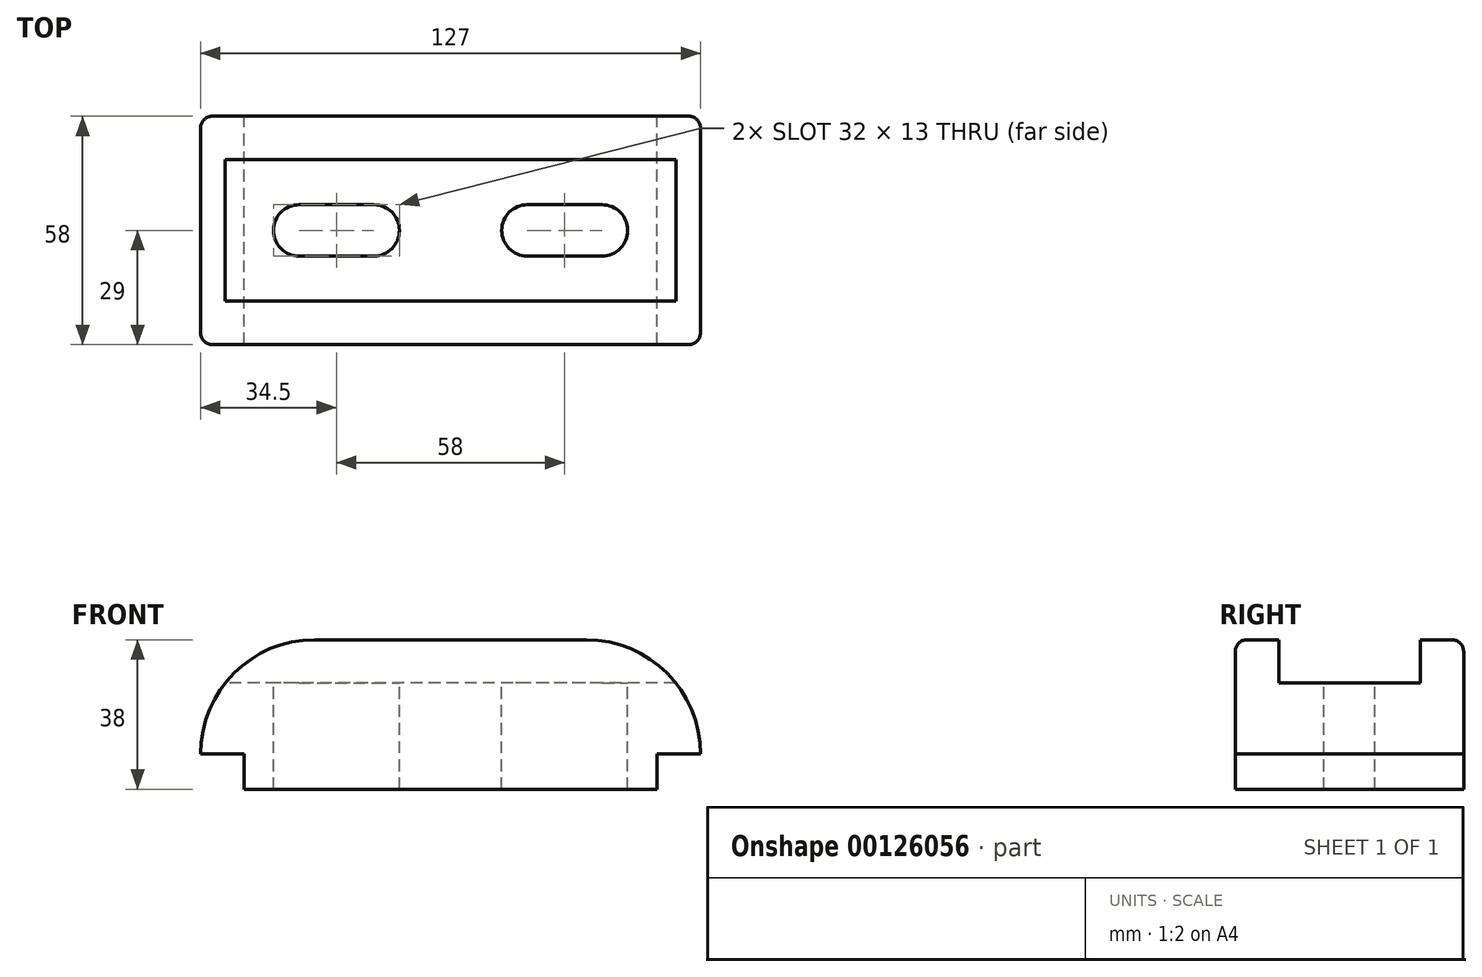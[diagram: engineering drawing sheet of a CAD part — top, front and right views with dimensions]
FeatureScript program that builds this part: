
annotation { "Feature Type Name" : "Feature", "Feature Type Description" : "" }
export const myFeature = defineFeature(function(context is Context, id is Id, definition is map)
    precondition{}
    {
        {
            var Q0;
            Q0=qCreatedBy(makeId("Front.planeOp"),FACE);
            var sketch = newSketch(context, id + "F0", { "sketchPlane" : qUnion([Q0])});
            skLineSegment(sketch, "E0", {"start": v(0, 0) * mm, "end": v(0, 9) * mm});
            skLineSegment(sketch, "E1", {"start": v(0, 9) * mm, "end": v(11, 9) * mm});
            skLineSegment(sketch, "E2", {"start": v(11, 9) * mm, "end": v(11, 9) * mm});
            skLineSegment(sketch, "E3", {"start": v(-18, 38) * mm, "end": v(-87, 38) * mm});
            skLineSegment(sketch, "E4", {"start": v(-116, 9) * mm, "end": v(-116, 9) * mm});
            skLineSegment(sketch, "E5", {"start": v(-116, 9) * mm, "end": v(-105, 9) * mm});
            skLineSegment(sketch, "E6", {"start": v(-105, 9) * mm, "end": v(-105, 0) * mm});
            skLineSegment(sketch, "E7", {"start": v(-105, 0) * mm, "end": v(0, 0) * mm});
            skPoint(sketch, "E8.visualSharp", {"position": v(-116, 38) * mm});
            skArc(sketch, "E8.filletArc", {"start": v(-87, 38) * mm, "mid": v(-107.5, 29.5) * mm, "end": v(-116, 9) * mm});
            skPoint(sketch, "E9.visualSharp", {"position": v(11, 38) * mm});
            skArc(sketch, "E9.filletArc", {"start": v(11, 9) * mm, "mid": v(2.5, 29.5) * mm, "end": v(-18, 38) * mm});
            skSolve(sketch);
        }
        {
            var Q0;
            Q0 = qSketchRegion(id + "F0", true);
            extrude(context, id + "F1", {"entities" : qUnion([Q0]), "endBound" : BoundingType.SYMMETRIC, "depth" : 58 * mm});
        }
        {
            var Q0;
            Q0=makeQuery(id+"F1.opExtrude","SWEPT_FACE",FACE,{"disambiguationData":[OSD([sQuery(id+"F0.wireOp",EDGE,"E3")])]});
            var sketch = newSketch(context, id + "F2", { "sketchPlane" : qUnion([Q0])});
            skLineSegment(sketch, "E10", {"start": v(-128, 18) * mm, "end": v(22, 18) * mm});
            skLineSegment(sketch, "E11", {"start": v(22, 18) * mm, "end": v(22, -18) * mm});
            skLineSegment(sketch, "E12", {"start": v(22, -18) * mm, "end": v(-128, -18) * mm});
            skLineSegment(sketch, "E13", {"start": v(-128, -18) * mm, "end": v(-128, 18) * mm});
            skSolve(sketch);
        }
        {
            var Q0;
            Q0 = qSketchRegion(id + "F2", true);
            extrude(context, id + "F3", {"entities" : qUnion([Q0]), "operationType" : NewBodyOperationType.REMOVE, "oppositeDirection" : true, "depth" : 11 * mm});
        }
        {
            var Q0;
            Q0=makeQuery(id+"F3.boolean.opBoolean","COPY",FACE,{"derivedFrom":makeQuery(id+"F3.opExtrude","CAP_FACE",FACE,{"disambiguationData":[OSD([sQuery(id+"F2.wireOp",EDGE,"E10"),sQuery(id+"F2.wireOp",EDGE,"E11"),sQuery(id+"F2.wireOp",EDGE,"E12"),sQuery(id+"F2.wireOp",EDGE,"E13")])],"isStart":false})});
            var sketch = newSketch(context, id + "F4", { "sketchPlane" : qUnion([Q0])});
            skArc(sketch, "E14", {"start": v(-14, -6.5) * mm, "mid": v(-7.5, 0) * mm, "end": v(-14, 6.5) * mm});
            skArc(sketch, "E15", {"start": v(-33, 6.5) * mm, "mid": v(-39.5, 0) * mm, "end": v(-33, -6.5) * mm});
            skArc(sketch, "E16", {"start": v(-72, -6.5) * mm, "mid": v(-65.5, 0) * mm, "end": v(-72, 6.5) * mm});
            skArc(sketch, "E17", {"start": v(-91, 6.5) * mm, "mid": v(-97.5, 0) * mm, "end": v(-91, -6.5) * mm});
            skLineSegment(sketch, "E18", {"start": v(-91, 6.5) * mm, "end": v(-72, 6.5) * mm});
            skLineSegment(sketch, "E19", {"start": v(-72, -6.5) * mm, "end": v(-91, -6.5) * mm});
            skPoint(sketch, "E20", {"position": v(-91, 6.5) * mm});
            skPoint(sketch, "E21", {"position": v(-91, -6.5) * mm});
            skPoint(sketch, "E22", {"position": v(-72, 6.5) * mm});
            skPoint(sketch, "E23", {"position": v(-72, -6.5) * mm});
            skLineSegment(sketch, "E24", {"start": v(-14, 6.5) * mm, "end": v(-33, 6.5) * mm});
            skLineSegment(sketch, "E25", {"start": v(-14, -6.5) * mm, "end": v(-33, -6.5) * mm});
            skPoint(sketch, "E26", {"position": v(-33, 6.5) * mm});
            skPoint(sketch, "E27", {"position": v(-33, -6.5) * mm});
            skPoint(sketch, "E28", {"position": v(-14, 6.5) * mm});
            skPoint(sketch, "E29", {"position": v(-14, -6.5) * mm});
            skSolve(sketch);
        }
        {
            var Q0;
            Q0 = qSketchRegion(id + "F4", true);
            extrude(context, id + "F5", {"entities" : qUnion([Q0]), "operationType" : NewBodyOperationType.REMOVE, "endBound" : BoundingType.THROUGH_ALL, "oppositeDirection" : true, "depth" : 25 * mm});
        }
        {
            var Q0;
            Q0=makeQuery(id+"F1.opExtrude","CAP_EDGE",EDGE,{"disambiguationData":[OSD([sQuery(id+"F0.wireOp",EDGE,"E3")])],"isStart":false});
            var Q1;
            Q1=makeQuery(id+"F1.opExtrude","CAP_EDGE",EDGE,{"disambiguationData":[OSD([sQuery(id+"F0.wireOp",EDGE,"E3")])],"isStart":true});
            fillet(context, id + "F6", {"entities" : qUnion([Q0, Q1]), "radius" : 3 * mm, "tangentPropagation" : true, "allowEdgeOverflow" : false});
        }
    });
